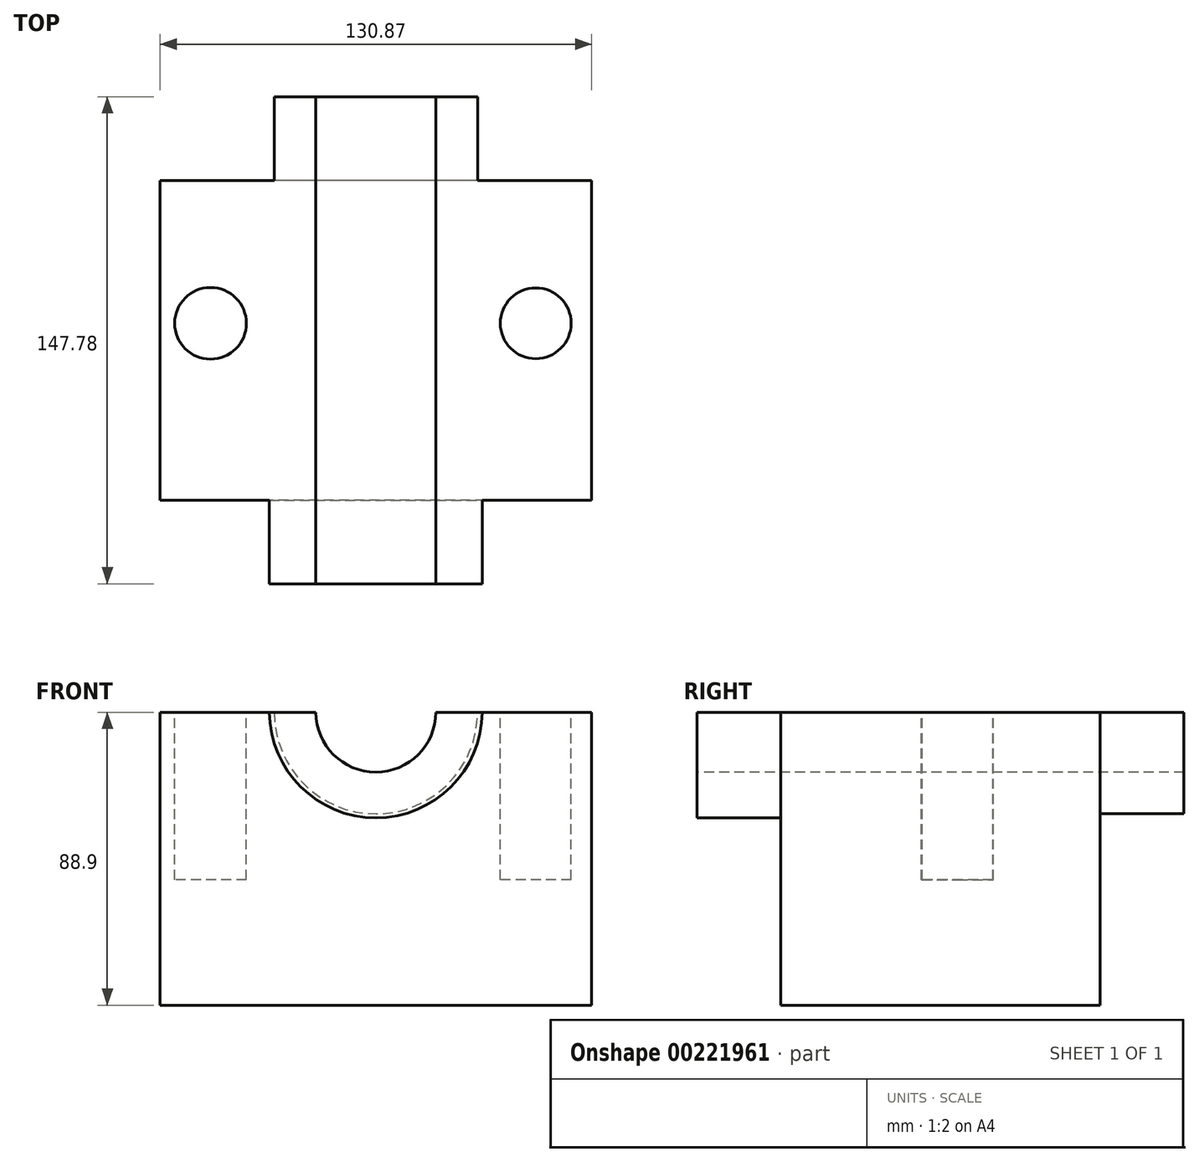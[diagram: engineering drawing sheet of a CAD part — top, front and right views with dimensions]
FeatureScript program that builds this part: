
annotation { "Feature Type Name" : "Feature", "Feature Type Description" : "" }
export const myFeature = defineFeature(function(context is Context, id is Id, definition is map)
    precondition{}
    {
        {
            var Q0;
            Q0=qCreatedBy(makeId("Top.planeOp"),FACE);
            var sketch = newSketch(context, id + "F0", { "sketchPlane" : qUnion([Q0])});
            skLineSegment(sketch, "E0.bottom", {"start": v(77.57, -77.96) * mm, "end": v(-53.3, -77.96) * mm});
            skLineSegment(sketch, "E0.top", {"start": v(77.57, 19.02) * mm, "end": v(-53.3, 19.02) * mm});
            skLineSegment(sketch, "E0.left", {"start": v(77.57, -77.96) * mm, "end": v(77.57, 19.02) * mm});
            skLineSegment(sketch, "E0.right", {"start": v(-53.3, -77.96) * mm, "end": v(-53.3, 19.02) * mm});
            skSolve(sketch);
        }
        {
            var Q0;
            Q0 = qSketchRegion(id + "F0", true);
            extrude(context, id + "F1", {"entities" : qUnion([Q0]), "depth" : 88.9 * mm});
        }
        {
            var Q0;
            Q0=makeQuery(id+"F1.opExtrude","SWEPT_FACE",FACE,{"disambiguationData":[OSD([sQuery(id+"F0.wireOp",EDGE,"E0.top")])]});
            var sketch = newSketch(context, id + "F2", { "sketchPlane" : qUnion([Q0])});
            skArc(sketch, "E1", {"start": v(-42.98, 88.9) * mm, "mid": v(-12.13, 58.05) * mm, "end": v(18.71, 88.9) * mm});
            skLineSegment(sketch, "E2", {"start": v(18.71, 88.9) * mm, "end": v(-42.98, 88.9) * mm});
            skSolve(sketch);
        }
        {
            var Q0;
            Q0 = qSketchRegion(id + "F2", true);
            extrude(context, id + "F3", {"entities" : qUnion([Q0]), "operationType" : NewBodyOperationType.ADD, "depth" : 25.4 * mm});
        }
        {
            var Q0;
            Q0=makeQuery(id+"F1.opExtrude","SWEPT_FACE",FACE,{"disambiguationData":[OSD([sQuery(id+"F0.wireOp",EDGE,"E0.bottom")])]});
            var sketch = newSketch(context, id + "F4", { "sketchPlane" : qUnion([Q0])});
            skArc(sketch, "E3", {"start": v(-20.18, 88.9) * mm, "mid": v(12.13, 56.87) * mm, "end": v(44.43, 88.9) * mm});
            skLineSegment(sketch, "E4", {"start": v(44.43, 88.9) * mm, "end": v(-20.18, 88.9) * mm});
            skSolve(sketch);
        }
        {
            var Q0;
            Q0 = qSketchRegion(id + "F4", true);
            extrude(context, id + "F5", {"entities" : qUnion([Q0]), "operationType" : NewBodyOperationType.ADD, "depth" : 25.4 * mm});
        }
        {
            var Q0;
            Q0=makeQuery(id+"F5.opExtrude","CAP_FACE",FACE,{"disambiguationData":[OSD([sQuery(id+"F4.wireOp",EDGE,"E3"),sQuery(id+"F4.wireOp",EDGE,"E4")])],"isStart":false});
            var sketch = newSketch(context, id + "F6", { "sketchPlane" : qUnion([Q0])});
            skCircle(sketch, "E5", {"center": v(12.13, 88.9) * mm, "radius": 18.19 * mm});
            skSolve(sketch);
        }
        {
            var Q0;
            Q0 = qSketchRegion(id + "F6", true);
            extrude(context, id + "F7", {"entities" : qUnion([Q0]), "operationType" : NewBodyOperationType.REMOVE, "endBound" : BoundingType.THROUGH_ALL, "oppositeDirection" : true, "depth" : 25.4 * mm});
        }
        {
            var Q0;
            {var subQ0=sQuery(id+"F0.wireOp",EDGE,"E0.left");var subQ1=sQuery(id+"F4.wireOp",EDGE,"E4");var subQ3=sQuery(id+"F0.wireOp",EDGE,"E0.top");var subQ5=sQuery(id+"F0.wireOp",EDGE,"E0.bottom");var subQ6=sQuery(id+"F2.wireOp",EDGE,"E2");Q0=makeQuery(id+"F7.boolean.opBoolean","SPLIT",FACE,{"disambiguationData":[TD([makeQuery(id+"F1.opExtrude","SWEPT_FACE",FACE,{"disambiguationData":[OSD([subQ0])]})])],"derivedFrom":makeQuery(id+"F5.boolean.opBoolean","MERGE",FACE,{"derivedFrom":[makeQuery(id+"F3.boolean.opBoolean","MERGE",FACE,{"derivedFrom":[makeQuery(id+"F1.opExtrude","CAP_FACE",FACE,{"disambiguationData":[OSD([subQ5,subQ3,subQ0,sQuery(id+"F0.wireOp",EDGE,"E0.right")])],"isStart":false}),makeQuery(id+"F3.opExtrude","SWEPT_FACE",FACE,{"disambiguationData":[OSD([subQ6])]})]}),makeQuery(id+"F5.opExtrude","SWEPT_FACE",FACE,{"disambiguationData":[OSD([subQ1])]})]})});}
            var sketch = newSketch(context, id + "F8", { "sketchPlane" : qUnion([Q0])});
            skCircle(sketch, "E6", {"center": v(60.65, -24.33) * mm, "radius": 10.74 * mm});
            skCircle(sketch, "E7", {"center": v(-38.03, -24.33) * mm, "radius": 10.88 * mm});
            skSolve(sketch);
        }
        {
            var Q0;
            Q0 = qSketchRegion(id + "F8", true);
            extrude(context, id + "F9", {"entities" : qUnion([Q0]), "operationType" : NewBodyOperationType.REMOVE, "oppositeDirection" : true, "depth" : 50.8 * mm});
        }
    });
